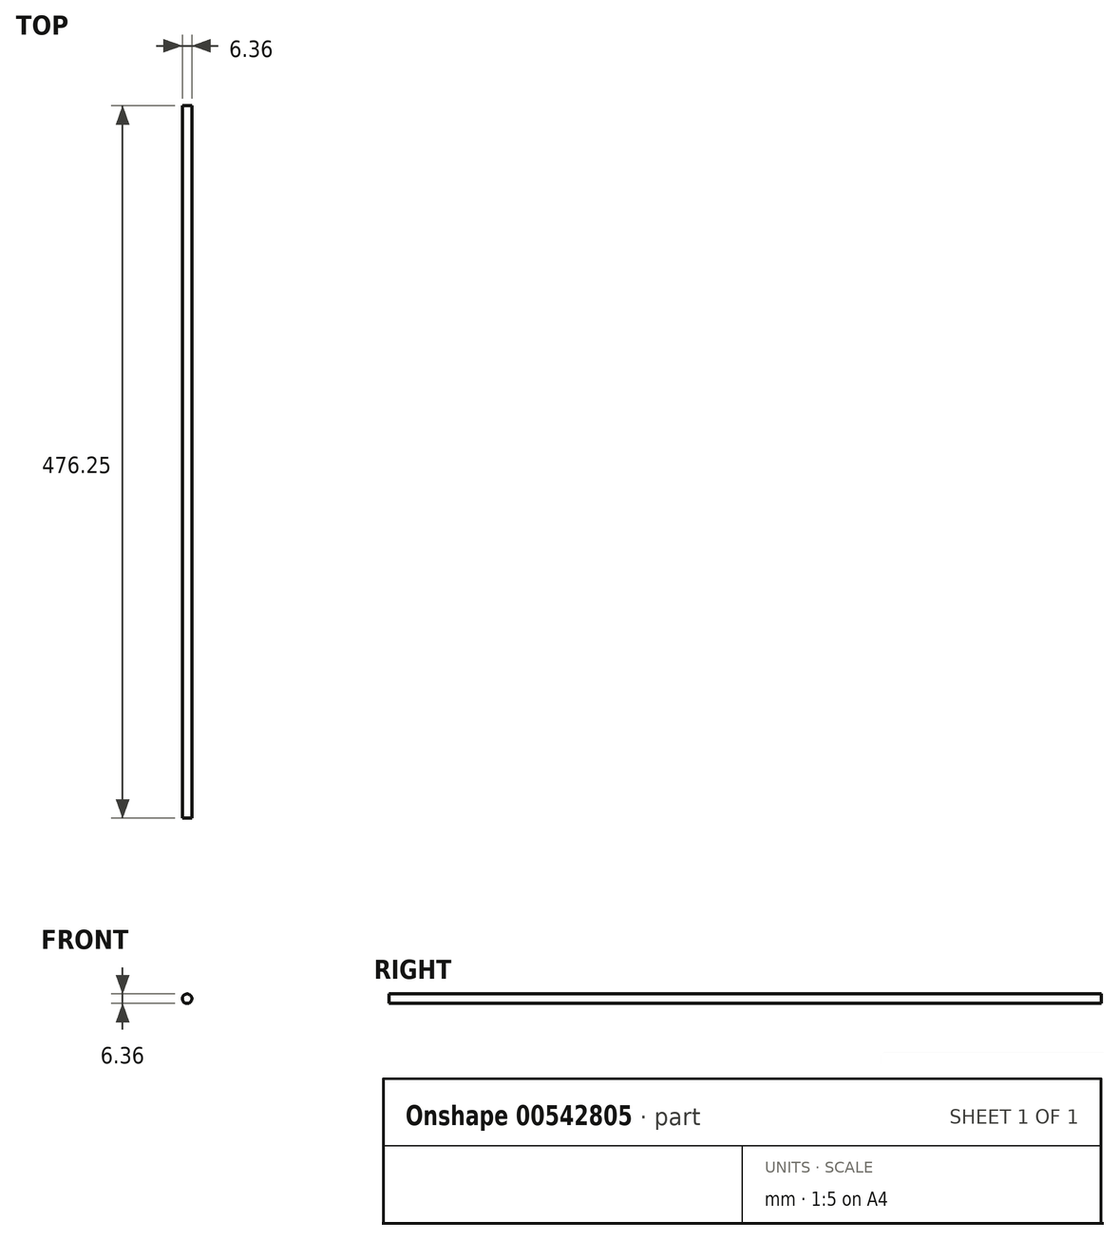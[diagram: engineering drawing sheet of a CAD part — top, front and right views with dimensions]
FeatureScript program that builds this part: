
annotation { "Feature Type Name" : "Feature", "Feature Type Description" : "" }
export const myFeature = defineFeature(function(context is Context, id is Id, definition is map)
    precondition{}
    {
        {
            var Q0;
            Q0=qCreatedBy(makeId("Front.planeOp"),FACE);
            var sketch = newSketch(context, id + "F0", { "sketchPlane" : qUnion([Q0])});
            skCircle(sketch, "E0", {"center": v(0, 0) * mm, "radius": 3.18 * mm});
            skSolve(sketch);
        }
        {
            var Q0;
            Q0=qSketchRegion(id+"F0",true);
            extrude(context, id + "F1", {"entities" : qUnion([Q0]), "depth" : 476.25 * mm, "offsetDistance" : 25.4 * mm});
        }
    });
